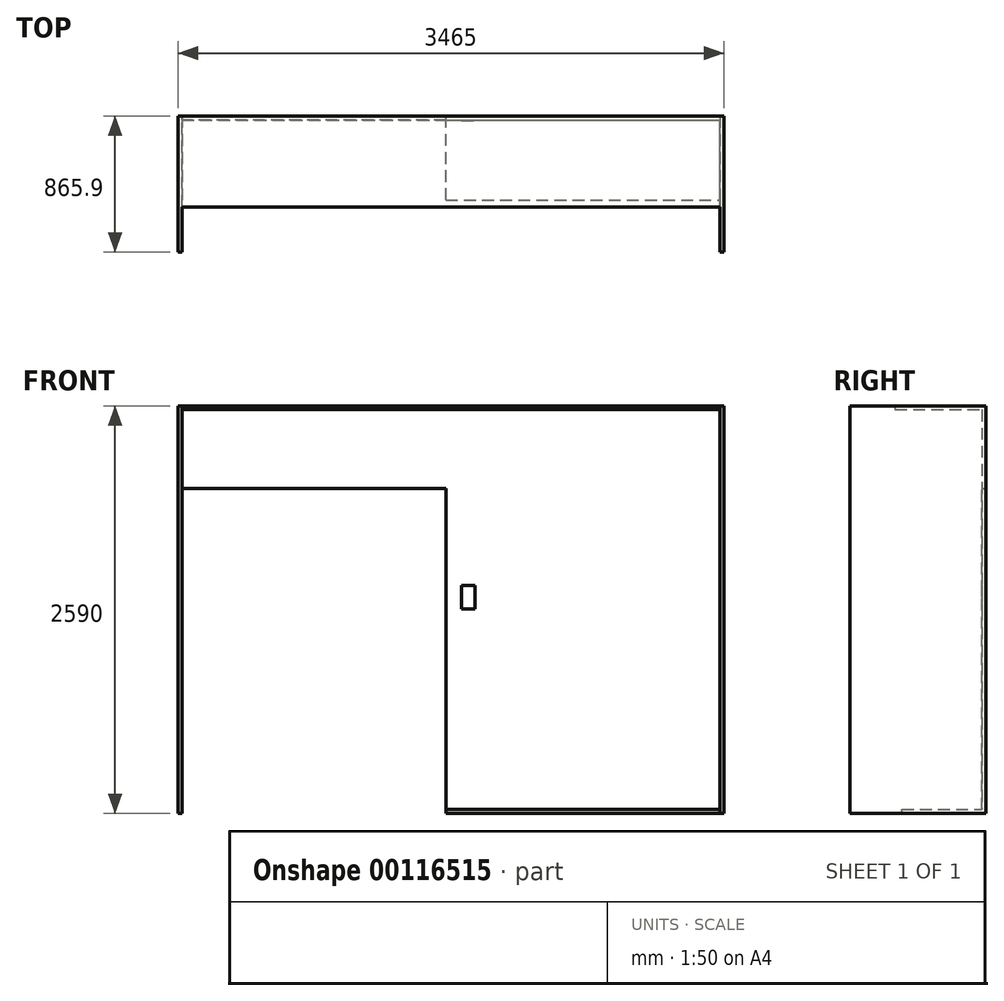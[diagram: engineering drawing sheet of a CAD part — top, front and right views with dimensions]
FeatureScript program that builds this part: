
annotation { "Feature Type Name" : "Feature", "Feature Type Description" : "" }
export const myFeature = defineFeature(function(context is Context, id is Id, definition is map)
    precondition{}
    {
        {
            var Q0;
            Q0=qCreatedBy(makeId("Front.planeOp"),FACE);
            var sketch = newSketch(context, id + "F0", { "sketchPlane" : qUnion([Q0])});
            skLineSegment(sketch, "E0.bottom", {"start": v(-109.29, 2467.86) * mm, "end": v(1890.71, 2467.86) * mm});
            skLineSegment(sketch, "E0.top", {"start": v(150.71, -72.14) * mm, "end": v(1890.71, -72.14) * mm});
            skLineSegment(sketch, "E0.left", {"start": v(-109.29, 2467.86) * mm, "end": v(-109.29, 1967.86) * mm});
            skLineSegment(sketch, "E0.right", {"start": v(1890.71, 2467.86) * mm, "end": v(1890.71, -72.14) * mm});
            skLineSegment(sketch, "E1", {"start": v(150.71, -72.14) * mm, "end": v(150.71, 1967.86) * mm});
            skLineSegment(sketch, "E2", {"start": v(150.71, 1967.86) * mm, "end": v(-109.29, 1967.86) * mm});
            skLineSegment(sketch, "E3.bottom", {"start": v(250.71, 1352.86) * mm, "end": v(335.71, 1352.86) * mm});
            skLineSegment(sketch, "E3.top", {"start": v(250.71, 1202.86) * mm, "end": v(335.71, 1202.86) * mm});
            skLineSegment(sketch, "E3.left", {"start": v(250.71, 1352.86) * mm, "end": v(250.71, 1202.86) * mm});
            skLineSegment(sketch, "E3.right", {"start": v(335.71, 1352.86) * mm, "end": v(335.71, 1202.86) * mm});
            skSolve(sketch);
        }
        {
            var Q0;
            Q0=makeQuery(id+"F0.imprint","IMPRINT",FACE,{"disambiguationData":[TD([[makeQuery(id+"F0.imprint","IMPRINT",EDGE,{"derivedFrom":sQuery(id+"F0.wireOp",EDGE,"E0.bottom")}),-1.0]])]});
            extrude(context, id + "F1", {"entities" : qUnion([Q0]), "depth" : 25 * mm});
        }
        {
            var Q0;
            Q0=makeQuery(id+"F0.imprint","IMPRINT",FACE,{"disambiguationData":[TD([[makeQuery(id+"F0.imprint","IMPRINT",EDGE,{"derivedFrom":sQuery(id+"F0.wireOp",EDGE,"E3.bottom")}),-1.0]])]});
            extrude(context, id + "F2", {"entities" : qUnion([Q0]), "operationType" : NewBodyOperationType.ADD, "depth" : 30 * mm});
        }
        {
            var Q0;
            Q0=makeQuery(id+"F1.opExtrude","SWEPT_FACE",FACE,{"disambiguationData":[OSD([sQuery(id+"F0.wireOp",EDGE,"E0.top")])]});
            var sketch = newSketch(context, id + "F3", { "sketchPlane" : qUnion([Q0])});
            skLineSegment(sketch, "E4.bottom", {"start": v(150.71, 0) * mm, "end": v(1890.71, 0) * mm});
            skLineSegment(sketch, "E4.top", {"start": v(150.71, 534.12) * mm, "end": v(1890.71, 534.12) * mm});
            skLineSegment(sketch, "E4.left", {"start": v(150.71, 0) * mm, "end": v(150.71, 534.12) * mm});
            skLineSegment(sketch, "E4.right", {"start": v(1890.71, 0) * mm, "end": v(1890.71, 534.12) * mm});
            skSolve(sketch);
        }
        {
            var Q0;
            Q0 = qSketchRegion(id + "F3", true);
            extrude(context, id + "F4", {"entities" : qUnion([Q0]), "operationType" : NewBodyOperationType.ADD, "depth" : 25 * mm});
        }
        {
            var Q0;
            Q0=makeQuery(id+"F1.opExtrude","SWEPT_FACE",FACE,{"disambiguationData":[OSD([sQuery(id+"F0.wireOp",EDGE,"E0.bottom")])]});
            var sketch = newSketch(context, id + "F5", { "sketchPlane" : qUnion([Q0])});
            skLineSegment(sketch, "E5.bottom", {"start": v(-109.29, 0) * mm, "end": v(1890.71, 0) * mm});
            skLineSegment(sketch, "E5.top", {"start": v(-109.29, -577.2) * mm, "end": v(1890.71, -577.2) * mm});
            skLineSegment(sketch, "E5.left", {"start": v(-109.29, 0) * mm, "end": v(-109.29, -577.2) * mm});
            skLineSegment(sketch, "E5.right", {"start": v(1890.71, 0) * mm, "end": v(1890.71, -577.2) * mm});
            skSolve(sketch);
        }
        {
            var Q0;
            {var subQ0=sQuery(id+"F5.wireOp",EDGE,"E5.top");Q0=makeQuery(id+"F5.imprint","IMPRINT",FACE,{"disambiguationData":[TD([[makeQuery(id+"F5.imprint","IMPRINT",EDGE,{"derivedFrom":subQ0}),1.0]])]});}
            extrude(context, id + "F6", {"entities" : qUnion([Q0]), "depth" : 25 * mm});
        }
        {
            var Q0;
            {var subQ0=sQuery(id+"F5.wireOp",EDGE,"E5.bottom");Q0=makeQuery(id+"F5.imprint","IMPRINT",FACE,{"disambiguationData":[TD([[makeQuery(id+"F5.imprint","IMPRINT",EDGE,{"derivedFrom":subQ0}),-1.0]])]});}
            extrude(context, id + "F7", {"entities" : qUnion([Q0]), "depth" : 25 * mm});
        }
        {
            var Q0;
            Q0=makeQuery(id+"F7.opExtrude","SWEPT_FACE",FACE,{"disambiguationData":[OSD([sQuery(id+"F5.wireOp",EDGE,"E5.right")])]});
            var sketch = newSketch(context, id + "F8", { "sketchPlane" : qUnion([Q0])});
            skLineSegment(sketch, "E6.bottom", {"start": v(0, 2492.86) * mm, "end": v(-865.9, 2492.86) * mm});
            skLineSegment(sketch, "E6.top", {"start": v(0, -96.67) * mm, "end": v(-865.9, -96.67) * mm});
            skLineSegment(sketch, "E6.left", {"start": v(0, 2492.86) * mm, "end": v(0, -96.67) * mm});
            skLineSegment(sketch, "E6.right", {"start": v(-865.9, 2492.86) * mm, "end": v(-865.9, -96.67) * mm});
            skSolve(sketch);
        }
        {
            var Q0;
            Q0 = qSketchRegion(id + "F8", true);
            extrude(context, id + "F9", {"entities" : qUnion([Q0]), "depth" : 25 * mm});
        }
        {
            var Q0;
            Q0=makeQuery(id+"F1.opExtrude","SWEPT_BODY",BODY,{"disambiguationData":[OSD([sQuery(id+"F0.wireOp",EDGE,"E0.bottom"),sQuery(id+"F0.wireOp",EDGE,"E0.top"),sQuery(id+"F0.wireOp",EDGE,"E0.left"),sQuery(id+"F0.wireOp",EDGE,"E0.right"),sQuery(id+"F0.wireOp",EDGE,"E1"),sQuery(id+"F0.wireOp",EDGE,"E2"),sQuery(id+"F0.wireOp",EDGE,"E3.bottom"),sQuery(id+"F0.wireOp",EDGE,"E3.top"),sQuery(id+"F0.wireOp",EDGE,"E3.left"),sQuery(id+"F0.wireOp",EDGE,"E3.right")])]});
            var Q1;
            Q1=makeQuery(id+"F9.opExtrude","SWEPT_BODY",BODY,{"disambiguationData":[OSD([sQuery(id+"F8.wireOp",EDGE,"E6.bottom"),sQuery(id+"F8.wireOp",EDGE,"E6.top"),sQuery(id+"F8.wireOp",EDGE,"E6.left"),sQuery(id+"F8.wireOp",EDGE,"E6.right")])]});
            var Q2;
            Q2=makeQuery(id+"F7.opExtrude","SWEPT_BODY",BODY,{"disambiguationData":[OSD([sQuery(id+"F0.wireOp",EDGE,"E0.bottom"),sQuery(id+"F5.wireOp",EDGE,"E5.bottom"),sQuery(id+"F5.wireOp",EDGE,"E5.left"),sQuery(id+"F5.wireOp",EDGE,"E5.right")])]});
            var Q3;
            Q3=makeQuery(id+"F6.opExtrude","SWEPT_BODY",BODY,{"disambiguationData":[OSD([sQuery(id+"F0.wireOp",EDGE,"E0.bottom"),sQuery(id+"F5.wireOp",EDGE,"E5.top"),sQuery(id+"F5.wireOp",EDGE,"E5.left"),sQuery(id+"F5.wireOp",EDGE,"E5.right")])]});
            booleanBodies(context, id + "F10", {"operationType" : BooleanOperationType.UNION, "tools" : qUnion([Q0, Q1, Q2, Q3])});
        }
        {
            var Q0;
            {var subQ0=sQuery(id+"F5.wireOp",EDGE,"E5.left");Q0=makeQuery(id+"F10.opBoolean","MERGE",FACE,{"derivedFrom":[makeQuery(id+"F1.opExtrude","SWEPT_FACE",FACE,{"disambiguationData":[OSD([sQuery(id+"F0.wireOp",EDGE,"E0.left")])]}),makeQuery(id+"F6.opExtrude","SWEPT_FACE",FACE,{"disambiguationData":[OSD([subQ0])]}),makeQuery(id+"F7.opExtrude","SWEPT_FACE",FACE,{"disambiguationData":[OSD([subQ0])]})]});}
            extrude(context, id + "F11", {"entities" : qUnion([Q0]), "operationType" : NewBodyOperationType.ADD, "depth" : 1415 * mm});
        }
        {
            var Q0;
            Q0=makeQuery(id+"F11.opExtrude","CAP_FACE",FACE,{"disambiguationData":[OSD([sQuery(id+"F0.wireOp",EDGE,"E0.left"),sQuery(id+"F5.wireOp",EDGE,"E5.left")])],"isStart":false});
            var sketch = newSketch(context, id + "F12", { "sketchPlane" : qUnion([Q0])});
            skLineSegment(sketch, "E7.bottom", {"start": v(0, 2492.86) * mm, "end": v(865.82, 2492.86) * mm});
            skLineSegment(sketch, "E7.top", {"start": v(0, -96.57) * mm, "end": v(865.82, -96.57) * mm});
            skLineSegment(sketch, "E7.left", {"start": v(0, 2492.86) * mm, "end": v(0, -96.57) * mm});
            skLineSegment(sketch, "E7.right", {"start": v(865.82, 2492.86) * mm, "end": v(865.82, -96.57) * mm});
            skSolve(sketch);
        }
        {
            var Q0;
            Q0 = qSketchRegion(id + "F12", true);
            extrude(context, id + "F13", {"entities" : qUnion([Q0]), "operationType" : NewBodyOperationType.ADD, "depth" : 25 * mm});
        }
    });
